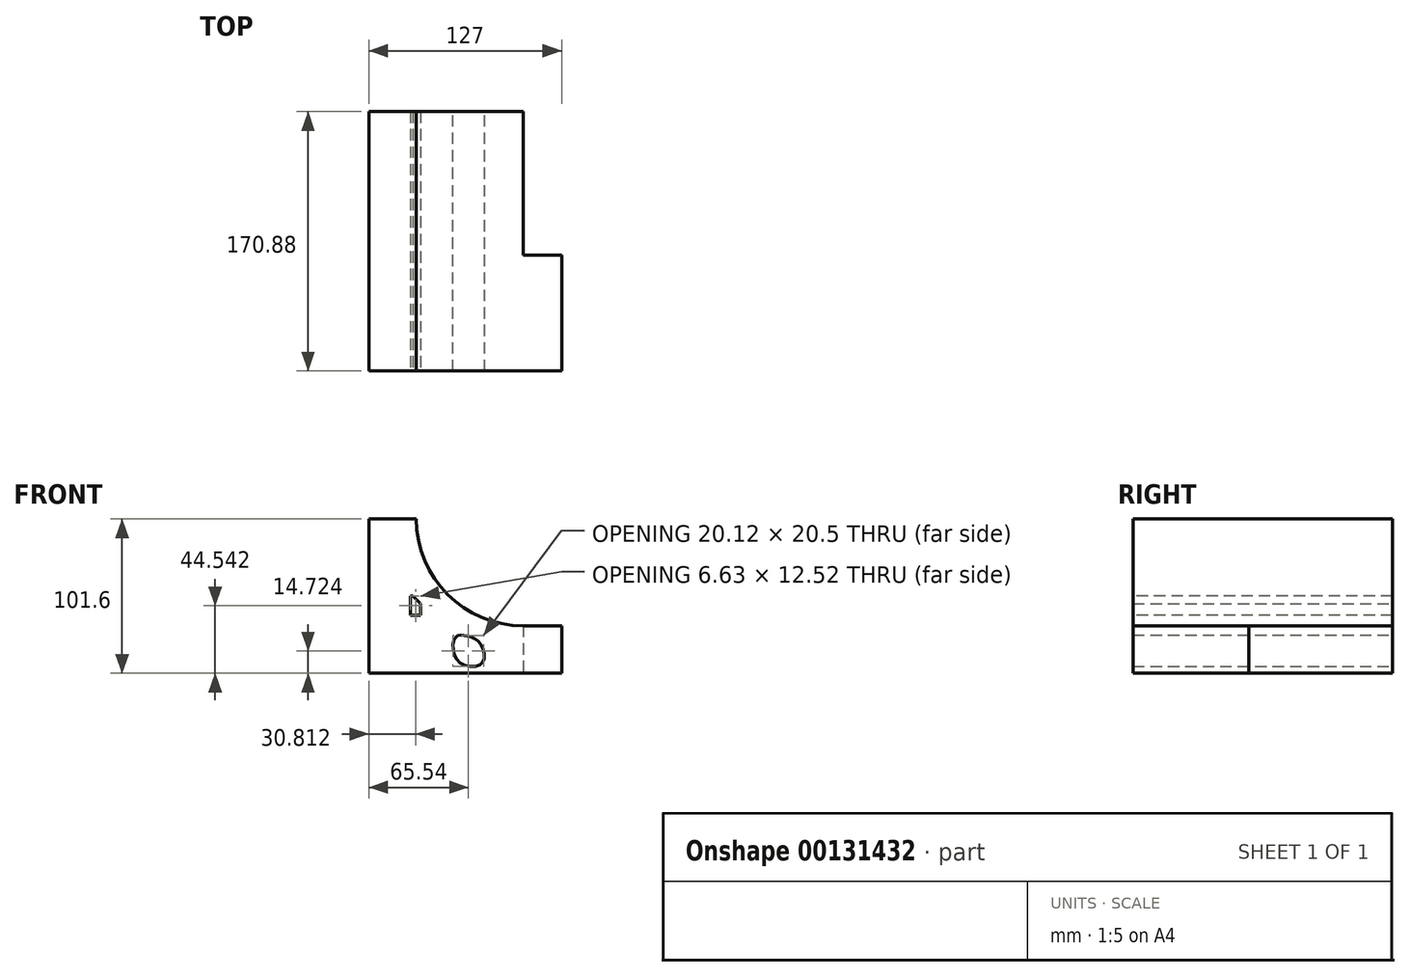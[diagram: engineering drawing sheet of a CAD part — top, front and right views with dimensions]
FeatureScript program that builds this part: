
annotation { "Feature Type Name" : "Feature", "Feature Type Description" : "" }
export const myFeature = defineFeature(function(context is Context, id is Id, definition is map)
    precondition{}
    {
        {
            var Q0;
            Q0=qCreatedBy(makeId("Front.planeOp"),FACE);
            var sketch = newSketch(context, id + "F9", { "sketchPlane" : qUnion([Q0])});
            skLineSegment(sketch, "E0.bottom", {"start": v(-101.6, 0) * mm, "end": v(0, 0) * mm});
            skLineSegment(sketch, "E0.top", {"start": v(-101.6, -101.6) * mm, "end": v(0, -101.6) * mm});
            skLineSegment(sketch, "E0.left", {"start": v(-101.6, 0) * mm, "end": v(-101.6, -101.6) * mm});
            skLineSegment(sketch, "E0.right", {"start": v(0, 0) * mm, "end": v(0, -101.6) * mm});
            skSolve(sketch);
        }
        {
            var Q0;
            Q0 = qSketchRegion(id + "F9", true);
            extrude(context, id + "F10", {"entities" : qUnion([Q0]), "depth" : 76.2 * mm});
        }
        {
            var Q0;
            Q0=makeQuery(id+"F10.opExtrude","CAP_FACE",FACE,{"disambiguationData":[OSD([sQuery(id+"F9.wireOp",EDGE,"E0.bottom"),sQuery(id+"F9.wireOp",EDGE,"E0.top"),sQuery(id+"F9.wireOp",EDGE,"E0.left"),sQuery(id+"F9.wireOp",EDGE,"E0.right")])],"isStart":false});
            var sketch = newSketch(context, id + "F0", { "sketchPlane" : qUnion([Q0])});
            skCircle(sketch, "E1", {"center": v(0, 0) * mm, "radius": 70.25 * mm});
            skSolve(sketch);
        }
        {
            var Q0;
            Q0=makeQuery(id+"F0.imprint","IMPRINT",FACE,{"disambiguationData":[TD([[makeQuery(id+"F0.imprint","IMPRINT",EDGE,{"derivedFrom":makeQuery(id+"F10.opExtrude","CAP_EDGE",EDGE,{"disambiguationData":[OSD([sQuery(id+"F9.wireOp",EDGE,"E0.bottom")])],"isStart":false})}),-1.0]])]});
            var sketch = newSketch(context, id + "F11", { "sketchPlane" : qUnion([Q0])});
            skCircle(sketch, "E2", {"center": v(-50.21, -49.83) * mm, "radius": 14.36 * mm});
            skSolve(sketch);
        }
        {
            var Q0;
            Q0 = qSketchRegion(id + "F0", true);
            extrude(context, id + "F1", {"entities" : qUnion([Q0]), "operationType" : NewBodyOperationType.REMOVE, "endBound" : BoundingType.THROUGH_ALL, "oppositeDirection" : true, "depth" : 25.4 * mm});
        }
        {
            var Q0;
            Q0=makeQuery(id+"F10.opExtrude","CAP_FACE",FACE,{"disambiguationData":[OSD([sQuery(id+"F9.wireOp",EDGE,"E0.bottom"),sQuery(id+"F9.wireOp",EDGE,"E0.top"),sQuery(id+"F9.wireOp",EDGE,"E0.left"),sQuery(id+"F9.wireOp",EDGE,"E0.right")])],"isStart":false});
            var sketch = newSketch(context, id + "F2", { "sketchPlane" : qUnion([Q0])});
            skPoint(sketch, "E3.firstSnap0", {"position": v(-101.6, -50.8) * mm});
            skLineSegment(sketch, "E3.bottom", {"start": v(-74.1, -50.8) * mm, "end": v(-67.47, -50.8) * mm});
            skLineSegment(sketch, "E3.top", {"start": v(-74.1, -63.32) * mm, "end": v(-67.47, -63.32) * mm});
            skLineSegment(sketch, "E3.left", {"start": v(-74.1, -50.8) * mm, "end": v(-74.1, -63.32) * mm});
            skLineSegment(sketch, "E3.right", {"start": v(-67.47, -50.8) * mm, "end": v(-67.47, -63.32) * mm});
            skSolve(sketch);
        }
        {
            var Q0;
            Q0 = qSketchRegion(id + "F2", true);
            extrude(context, id + "F12", {"entities" : qUnion([Q0]), "operationType" : NewBodyOperationType.REMOVE, "endBound" : BoundingType.THROUGH_ALL, "oppositeDirection" : true, "depth" : 25.4 * mm});
        }
        {
            var Q0;
            Q0=makeQuery(id+"F12.boolean.opBoolean","COPY",EDGE,{"derivedFrom":makeQuery(id+"F12.opExtrude","CAP_EDGE",EDGE,{"disambiguationData":[OSD([sQuery(id+"F2.wireOp",EDGE,"E3.right")])],"isStart":true})});
            var Q1;
            Q1=makeQuery(id+"F12.boolean.opBoolean","COPY",EDGE,{"derivedFrom":makeQuery(id+"F12.opExtrude","SWEPT_EDGE",EDGE,{"disambiguationData":[OSD([sQuery(id+"F2.wireOp",EDGE,"E3.bottom"),sQuery(id+"F2.wireOp",EDGE,"E3.right")])]})});
            var Q2;
            Q2=makeQuery(id+"F12.boolean.opBoolean","COPY",EDGE,{"derivedFrom":makeQuery(id+"F12.opExtrude","CAP_EDGE",EDGE,{"disambiguationData":[OSD([sQuery(id+"F2.wireOp",EDGE,"E3.left")])],"isStart":true})});
            var Q3;
            Q3=makeQuery(id+"F12.boolean.opBoolean","COPY",EDGE,{"derivedFrom":makeQuery(id+"F12.opExtrude","CAP_EDGE",EDGE,{"disambiguationData":[OSD([sQuery(id+"F2.wireOp",EDGE,"E3.top")])],"isStart":true})});
            chamfer(context, id + "F13", {"entities" : qUnion([Q0, Q1, Q2, Q3]), "width" : 5.08 * mm, "tangentPropagation" : true});
        }
        {
            var Q0;
            Q0=sQuery(id+"F11.wireOp",EDGE,"E2");
            extrude(context, id + "F14", {"bodyType" : ToolBodyType.SURFACE, "surfaceEntities" : qUnion([Q0]), "oppositeDirection" : true, "depth" : 25.58 * mm});
        }
        {
            var Q0;
            Q0=makeQuery(id+"F10.opExtrude","CAP_FACE",FACE,{"disambiguationData":[OSD([sQuery(id+"F9.wireOp",EDGE,"E0.bottom"),sQuery(id+"F9.wireOp",EDGE,"E0.top"),sQuery(id+"F9.wireOp",EDGE,"E0.left"),sQuery(id+"F9.wireOp",EDGE,"E0.right")])],"isStart":false});
            var sketch = newSketch(context, id + "F3", { "sketchPlane" : qUnion([Q0])});
            skFitSpline(sketch, "E4", {"points": [v(-38.96, -76.63) * mm, v(-44.72, -78.22) * mm, v(-42.95, -93.28) * mm, v(-27.05, -95) * mm, v(-28.52, -81.66) * mm, v(-38.96, -76.63) * mm]});
            skSolve(sketch);
        }
        {
            var Q0;
            Q0 = qSketchRegion(id + "F3", true);
            extrude(context, id + "F4", {"entities" : qUnion([Q0]), "operationType" : NewBodyOperationType.REMOVE, "oppositeDirection" : true, "depth" : 98.45 * mm});
        }
        {
            var Q0;
            Q0=makeQuery(id+"F10.opExtrude","SWEPT_FACE",FACE,{"disambiguationData":[OSD([sQuery(id+"F9.wireOp",EDGE,"E0.right")])]});
            var sketch = newSketch(context, id + "F5", { "sketchPlane" : qUnion([Q0])});
            skSolve(sketch);
        }
        {
            var Q0;
            Q0=makeQuery(id+"F10.opExtrude","CAP_FACE",FACE,{"disambiguationData":[OSD([sQuery(id+"F9.wireOp",EDGE,"E0.bottom"),sQuery(id+"F9.wireOp",EDGE,"E0.top"),sQuery(id+"F9.wireOp",EDGE,"E0.left"),sQuery(id+"F9.wireOp",EDGE,"E0.right")])],"isStart":true});
            var sketch = newSketch(context, id + "F15", { "sketchPlane" : qUnion([Q0])});
            skSolve(sketch);
        }
        {
            var Q0;
            Q0 = qSketchRegion(id + "F15", true);
            var Q1;
            {var subQ3=sQuery(id+"F9.wireOp",EDGE,"E0.top");Q1=makeQuery(id+"F15.imprint","IMPRINT",FACE,{"disambiguationData":[TD([[makeQuery(id+"F15.imprint","IMPRINT",EDGE,{"derivedFrom":makeQuery(id+"F10.opExtrude","CAP_EDGE",EDGE,{"disambiguationData":[OSD([subQ3])],"isStart":true})}),-1.0]])]});}
            extrude(context, id + "F16", {"entities" : qUnion([Q0, Q1]), "operationType" : NewBodyOperationType.ADD, "depth" : 94.68 * mm});
        }
        {
            var Q0;
            {var subQ0=sQuery(id+"F9.wireOp",EDGE,"E0.right");Q0=makeQuery(id+"F5.imprint","IMPRINT",FACE,{"disambiguationData":[TD([[makeQuery(id+"F5.imprint","IMPRINT",EDGE,{"derivedFrom":makeQuery(id+"F10.opExtrude","CAP_EDGE",EDGE,{"disambiguationData":[OSD([subQ0])],"isStart":true})}),-1.0]])]});}
            var sketch = newSketch(context, id + "F6", { "sketchPlane" : qUnion([Q0])});
            skCircle(sketch, "E5", {"center": v(-34.8, -99.74) * mm, "radius": 2.26 * mm});
            skCircle(sketch, "E6", {"center": v(-40.48, -92.04) * mm, "radius": 5.23 * mm});
            skSolve(sketch);
        }
        {
            var Q0;
            {var subQ0=sQuery(id+"F9.wireOp",EDGE,"E0.right");Q0=makeQuery(id+"F5.imprint","IMPRINT",FACE,{"disambiguationData":[TD([[makeQuery(id+"F5.imprint","IMPRINT",EDGE,{"derivedFrom":makeQuery(id+"F10.opExtrude","CAP_EDGE",EDGE,{"disambiguationData":[OSD([subQ0])],"isStart":true})}),-1.0]])]});}
            extrude(context, id + "F7", {"entities" : qUnion([Q0]), "operationType" : NewBodyOperationType.ADD, "depth" : 25.4 * mm});
        }
        {
            var Q0;
            Q0=sQuery(id+"F6.wireOp",EDGE,"E6");
            extrude(context, id + "F8", {"bodyType" : ToolBodyType.SURFACE, "surfaceEntities" : qUnion([Q0]), "depth" : 127 * mm});
        }
    });
